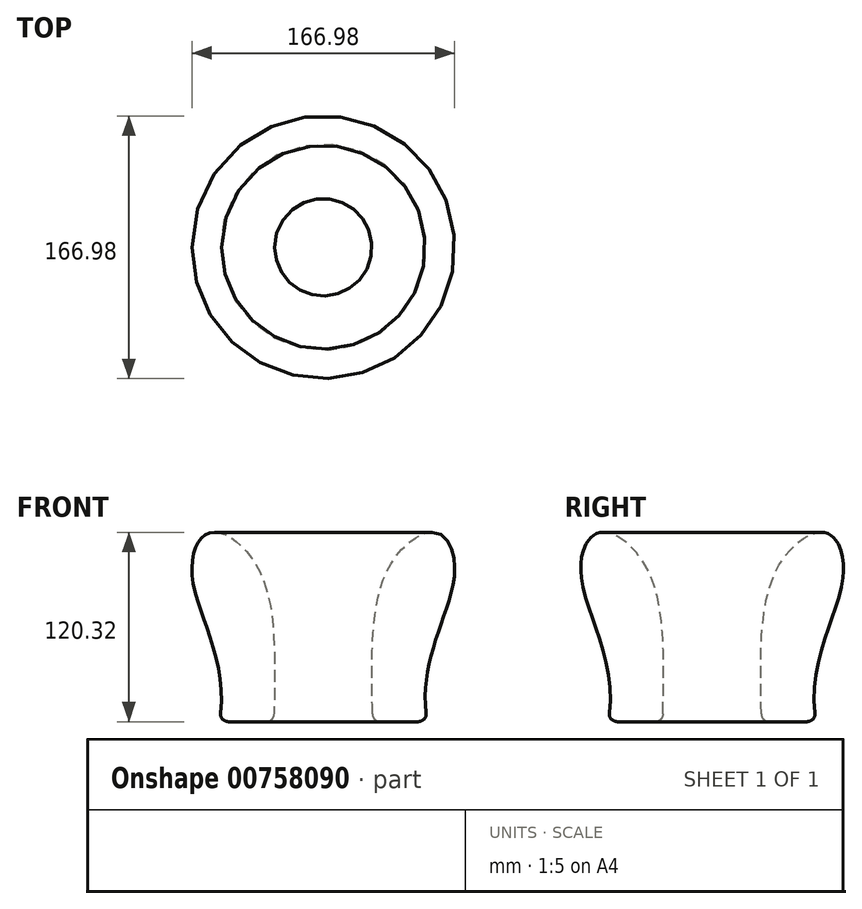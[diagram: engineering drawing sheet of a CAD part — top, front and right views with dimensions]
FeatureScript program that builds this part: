
annotation { "Feature Type Name" : "Feature", "Feature Type Description" : "" }
export const myFeature = defineFeature(function(context is Context, id is Id, definition is map)
    precondition{}
    {
        {
            var Q0;
            Q0=qCreatedBy(makeId("Front.planeOp"),FACE);
            var sketch = newSketch(context, id + "F0", { "sketchPlane" : qUnion([Q0])});
            skFitSpline(sketch, "E0", {"points": [v(-66.22, 0) * mm, v(-83.22, 92.04) * mm, v(-71.82, 120) * mm, v(-41.22, 97.1) * mm, v(-31.24, 0) * mm], "startDerivative": vector(71.5, 355.62) * mm, "endDerivative": vector(-3.04, -360.62) * mm});
            skLineSegment(sketch, "E1", {"start": v(-66.22, 0) * mm, "end": v(-31.22, 0) * mm});
            skLineSegment(sketch, "E2", {"start": v(-31.24, 0) * mm, "end": v(-31.24, 0) * mm});
            skLineSegment(sketch, "E3", {"start": v(0, -15.56) * mm, "end": v(0, 129.82) * mm});
            skSolve(sketch);
        }
        {
            var Q0;
            Q0=makeQuery(id+"F0.imprint","IMPRINT",FACE,{"disambiguationData":[TD([[makeQuery(id+"F0.imprint","IMPRINT",EDGE,{"derivedFrom":sQuery(id+"F0.wireOp",EDGE,"E0")}),-1.0]])]});
            var Q1;
            Q1=sQuery(id+"F0.wireOp",EDGE,"E3");
            revolve(context, id + "F1", {"surfaceOperationType" : NewSurfaceOperationType.NEW, "entities" : qUnion([Q0]), "axis" : qUnion([Q1]), "revolveType" : RevolveType.FULL});
        }
        {
            var Q0;
            Q0=makeQuery(id+"F1.opRevolve","SWEPT_EDGE",EDGE,{"disambiguationData":[OSD([sQuery(id+"F0.wireOp",EDGE,"E1"),sQuery(id+"F0.wireOp",EDGE,"E2")])]});
            var Q1;
            Q1=makeQuery(id+"F1.opRevolve","SWEPT_EDGE",EDGE,{"disambiguationData":[OSD([sQuery(id+"F0.wireOp",EDGE,"E0"),sQuery(id+"F0.wireOp",EDGE,"E1")])]});
            fillet(context, id + "F2", {"entities" : qUnion([Q0, Q1]), "radius" : 5 * mm, "tangentPropagation" : true, "allowEdgeOverflow" : false});
        }
    });
